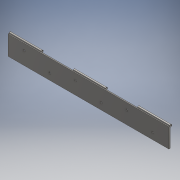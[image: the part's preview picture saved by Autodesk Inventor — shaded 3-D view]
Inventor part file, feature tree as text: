
AUTODESK INVENTOR PART (.ipt)
format: ipt  version: 2018 (Build 220112000, 112)  size: 165,376 bytes
history: native  units: mm
features: extrude x5, sketch x5, plane x1, hole x1
ambient origin geometry x8: Origin, YZ Plane, XZ Plane, XY Plane, X Axis, Y Axis, Z Axis, Center Point
bodies: Solid1 (feature_tree)
feature tree (12):
  extrude  "Extrusion1"  Depth=30.0mm
  sketch  "Sketch2"  dims[d2=2.0mm d3=0.0mm d4=2.5mm]
  extrude  "Extrusion2"  Depth=2.0mm
  extrude  "Extrusion3"  Depth=3.5mm
  sketch  "Sketch3"  dims[d5=3.0mm d6=3.5mm]
  plane  "Work Plane1"
  hole  "Hole1"  [1 undecoded]
  extrude  "Extrusion6"  Depth=10.0mm
  extrude  "Extrusion7"  Depth=10.0mm
  sketch  "Sketch1"  dims[d0=250.0mm d1=30.0mm]
  sketch  "Sketch5"  dims[d7=250.0mm d8=0.0mm d9=250.0mm d10=0.0mm]
  sketch  "Sketch6"  dims[d23=40.0mm d24=5.0mm d25=40.0mm d26=40.0mm d27=40.0mm d28=40.0mm d29=10.0mm d30=10.0mm d31=3.0mm d32=6.0mm d33=5.0mm d34=2.0mm d35=90.0deg d36=8.0mm d37=20.594885mm d38=50.0mm d39=2.75mm d40=50.0mm d41=2.75mm d42=50.0mm d43=50.0mm d44=250.0mm d45=0.0mm d46=10.0mm d47=0.0mm]
note: 1 required parameter value undecoded (feature->parameter linkage not recoverable at this tier; creation-order binding heuristic only, values carry confidence <= 0.55)
